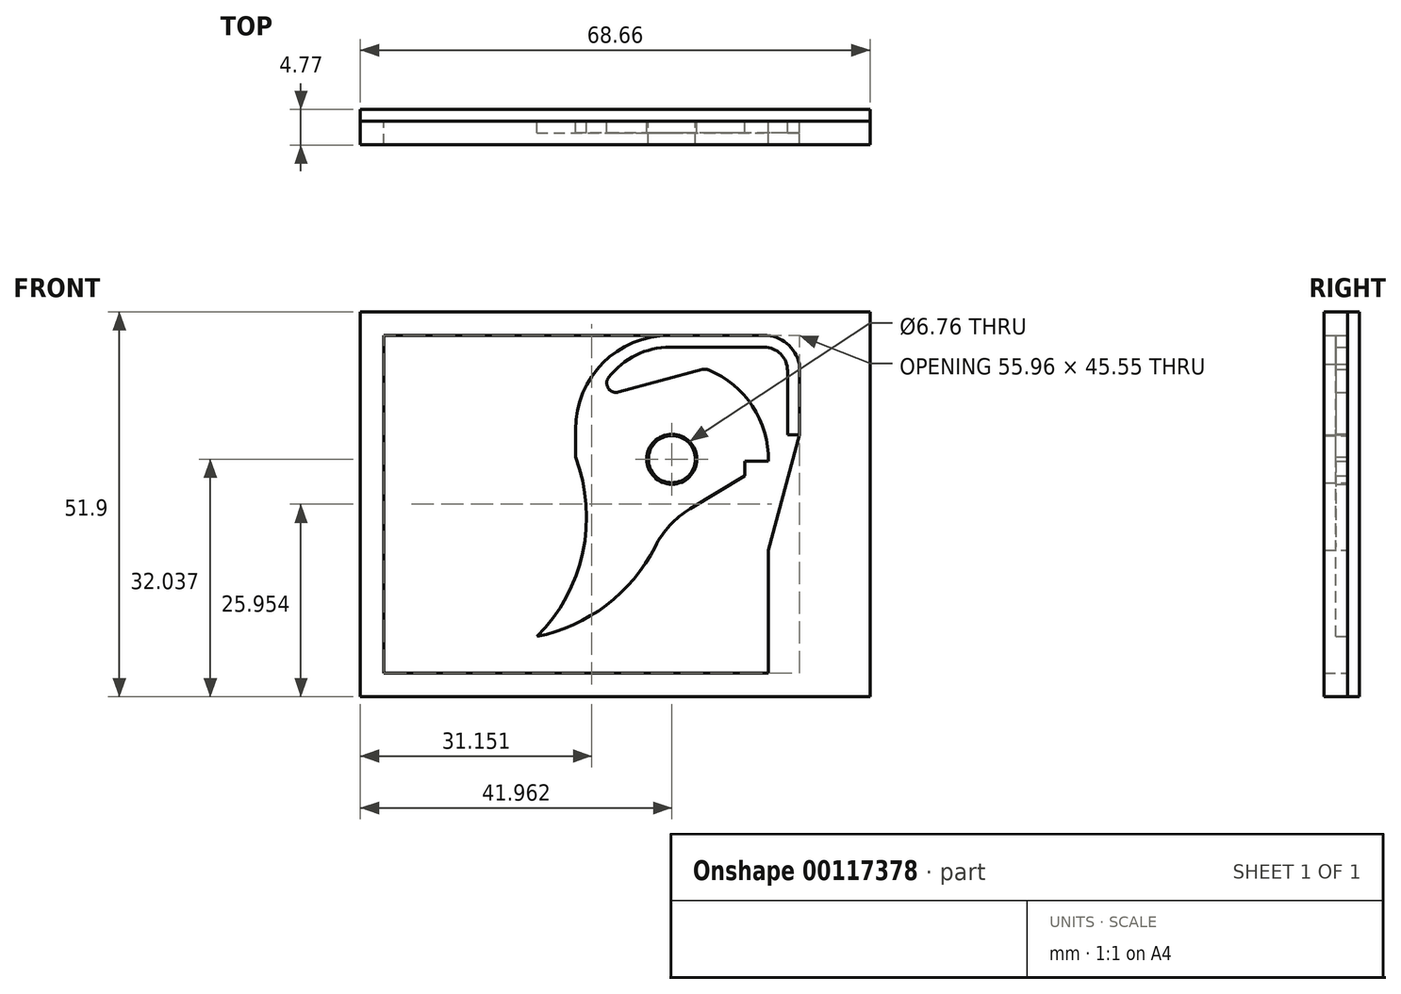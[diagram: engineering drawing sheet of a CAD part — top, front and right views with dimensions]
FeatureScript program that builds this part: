
annotation { "Feature Type Name" : "Feature", "Feature Type Description" : "" }
export const myFeature = defineFeature(function(context is Context, id is Id, definition is map)
    precondition{}
    {
        {
            var Q0;
            Q0=qCreatedBy(makeId("Front.planeOp"),FACE);
            var sketch = newSketch(context, id + "F0", { "sketchPlane" : qUnion([Q0])});
            skLineSegment(sketch, "E0.bottom", {"start": v(0, 0) * mm, "end": v(47.63, 0) * mm});
            skLineSegment(sketch, "E0.right", {"start": v(47.63, 0) * mm, "end": v(47.63, 16.58) * mm});
            skArc(sketch, "E1", {"start": v(16.43, 4.93) * mm, "mid": v(22.62, 16.26) * mm, "end": v(21.64, 29.14) * mm});
            skArc(sketch, "E2", {"start": v(16.43, 4.93) * mm, "mid": v(25.79, 9.17) * mm, "end": v(32.37, 17.06) * mm});
            skArc(sketch, "E3", {"start": v(47.62, 28.57) * mm, "mid": v(45.38, 36.16) * mm, "end": v(39.15, 41.04) * mm});
            skLineSegment(sketch, "E4", {"start": v(44.45, 26.64) * mm, "end": v(37.08, 22.15) * mm});
            skPoint(sketch, "E5.newPointB", {"position": v(34.83, 28.77) * mm});
            skArc(sketch, "E5.filletArc", {"start": v(37.08, 22.15) * mm, "mid": v(34.37, 19.93) * mm, "end": v(32.37, 17.06) * mm});
            skCircle(sketch, "E6", {"center": v(34.63, 28.86) * mm, "radius": 3.18 * mm});
            skLineSegment(sketch, "E7", {"start": v(21.64, 29.14) * mm, "end": v(21.64, 32.85) * mm});
            skLineSegment(sketch, "E8", {"start": v(34.34, 45.55) * mm, "end": v(47.04, 45.55) * mm});
            skPoint(sketch, "E9.visualSharp", {"position": v(21.64, 45.55) * mm});
            skArc(sketch, "E9.filletArc", {"start": v(34.34, 45.55) * mm, "mid": v(25.36, 41.83) * mm, "end": v(21.64, 32.85) * mm});
            skLineSegment(sketch, "E10.0", {"start": v(34.4, 43.96) * mm, "end": v(47.04, 43.96) * mm});
            skLineSegment(sketch, "E11", {"start": v(47.04, 45.55) * mm, "end": v(47.04, 43.96) * mm});
            skArc(sketch, "E12", {"start": v(34.4, 43.96) * mm, "mid": v(28.42, 42.08) * mm, "end": v(24.6, 37.11) * mm});
            skLineSegment(sketch, "E13", {"start": v(44.45, 28.58) * mm, "end": v(44.45, 26.64) * mm});
            skLineSegment(sketch, "E14", {"start": v(47.63, 28.57) * mm, "end": v(44.45, 28.57) * mm});
            skLineSegment(sketch, "E15", {"start": v(51.8, 41.64) * mm, "end": v(51.8, 32.11) * mm});
            skLineSegment(sketch, "E16.0", {"start": v(50.21, 40.79) * mm, "end": v(50.21, 32.11) * mm});
            skLineSegment(sketch, "E17", {"start": v(50.21, 32.11) * mm, "end": v(51.8, 32.11) * mm});
            skArc(sketch, "E18.filletArc", {"start": v(50.21, 40.79) * mm, "mid": v(49.28, 43.03) * mm, "end": v(47.04, 43.96) * mm});
            skArc(sketch, "E19", {"start": v(51.8, 41.64) * mm, "mid": v(50.12, 44.45) * mm, "end": v(47.04, 45.55) * mm});
            skLineSegment(sketch, "E20", {"start": v(24.6, 37.11) * mm, "end": v(39.15, 41.04) * mm});
            skLineSegment(sketch, "E21.bottom", {"start": v(-4.16, 0) * mm, "end": v(58.15, 0) * mm});
            skLineSegment(sketch, "E21.top", {"start": v(-4.16, 45.55) * mm, "end": v(58.15, 45.55) * mm});
            skLineSegment(sketch, "E21.left", {"start": v(-4.16, 0) * mm, "end": v(-4.16, 45.55) * mm});
            skLineSegment(sketch, "E21.right", {"start": v(58.15, 0) * mm, "end": v(58.15, 45.55) * mm});
            skCircle(sketch, "E22.0", {"center": v(34.63, 28.86) * mm, "radius": 3.38 * mm});
            skLineSegment(sketch, "E23", {"start": v(44.45, 26.64) * mm, "end": v(47.63, 16.58) * mm});
            skLineSegment(sketch, "E24", {"start": v(51.8, 32.11) * mm, "end": v(47.62, 16.58) * mm});
            skLineSegment(sketch, "E25.bottom", {"start": v(-7.33, -3.18) * mm, "end": v(61.33, -3.17) * mm});
            skLineSegment(sketch, "E25.top", {"start": v(-7.33, 48.72) * mm, "end": v(61.33, 48.72) * mm});
            skLineSegment(sketch, "E25.left", {"start": v(-7.33, -3.18) * mm, "end": v(-7.33, 48.72) * mm});
            skLineSegment(sketch, "E25.right", {"start": v(61.33, -3.17) * mm, "end": v(61.33, 48.72) * mm});
            skSolve(sketch);
        }
        {
            var Q0;
            Q0=makeQuery(id+"F0.imprint","IMPRINT",FACE,{"disambiguationData":[TD([[makeQuery(id+"F0.imprint","IMPRINT",EDGE,{"derivedFrom":sQuery(id+"F0.wireOp",EDGE,"E1")}),-1.0]])]});
            var Q1;
            Q1=makeQuery(id+"F0.imprint","IMPRINT",FACE,{"disambiguationData":[TD([[makeQuery(id+"F0.imprint","IMPRINT",EDGE,{"derivedFrom":sQuery(id+"F0.wireOp",EDGE,"E11")}),1.0]])]});
            extrude(context, id + "F1", {"entities" : qUnion([Q0, Q1]), "depth" : 1.59 * mm});
        }
        {
            var Q0;
            Q0=makeQuery(id+"F1.opExtrude","SWEPT_EDGE",EDGE,{"disambiguationData":[OSD([sQuery(id+"F0.wireOp",EDGE,"E3"),sQuery(id+"F0.wireOp",EDGE,"E12"),sQuery(id+"F0.wireOp",EDGE,"E20")])]});
            fillet(context, id + "F2", {"entities" : qUnion([Q0]), "radius" : 1.27 * mm, "tangentPropagation" : true, "allowEdgeOverflow" : false});
        }
        {
            var Q0;
            {var subQ0=sQuery(id+"F0.wireOp",EDGE,"E21.left");Q0=makeQuery(id+"F0.imprint","IMPRINT",FACE,{"disambiguationData":[TD([[makeQuery(id+"F0.imprint","IMPRINT",EDGE,{"derivedFrom":subQ0}),1.0]])]});}
            var Q1;
            {var subQ1=sQuery(id+"F0.wireOp",EDGE,"E0.right");Q1=makeQuery(id+"F0.imprint","IMPRINT",FACE,{"disambiguationData":[TD([[makeQuery(id+"F0.imprint","IMPRINT",EDGE,{"derivedFrom":subQ1}),-1.0]])]});}
            var Q2;
            {var subQ0=sQuery(id+"F0.wireOp",EDGE,"E0.right");Q2=makeQuery(id+"F0.imprint","IMPRINT",FACE,{"disambiguationData":[TD([[makeQuery(id+"F0.imprint","IMPRINT",EDGE,{"derivedFrom":subQ0}),1.0]])]});}
            var Q3;
            Q3=makeQuery(id+"F0.imprint","IMPRINT",FACE,{"disambiguationData":[TD([[makeQuery(id+"F0.imprint","IMPRINT",EDGE,{"derivedFrom":sQuery(id+"F0.wireOp",EDGE,"E3")}),-1.0]])]});
            var Q4;
            Q4=makeQuery(id+"F0.imprint","IMPRINT",FACE,{"disambiguationData":[TD([[makeQuery(id+"F0.imprint","IMPRINT",EDGE,{"derivedFrom":sQuery(id+"F0.wireOp",EDGE,"E6")}),-1.0]])]});
            var Q5;
            Q5=makeQuery(id+"F0.imprint","IMPRINT",FACE,{"disambiguationData":[TD([[makeQuery(id+"F0.imprint","IMPRINT",EDGE,{"derivedFrom":sQuery(id+"F0.wireOp",EDGE,"E6")}),1.0]])]});
            var Q6;
            Q6=makeQuery(id+"F0.imprint","IMPRINT",FACE,{"disambiguationData":[TD([[makeQuery(id+"F0.imprint","IMPRINT",EDGE,{"derivedFrom":sQuery(id+"F0.wireOp",EDGE,"E1")}),-1.0]])]});
            var Q7;
            Q7=makeQuery(id+"F0.imprint","IMPRINT",FACE,{"disambiguationData":[TD([[makeQuery(id+"F0.imprint","IMPRINT",EDGE,{"derivedFrom":sQuery(id+"F0.wireOp",EDGE,"E11")}),1.0]])]});
            extrude(context, id + "F3", {"entities" : qUnion([Q0, Q1, Q2, Q3, Q4, Q5, Q6, Q7]), "oppositeDirection" : true, "depth" : 1.59 * mm});
        }
        {
            var Q0;
            {var subQ0=sQuery(id+"F0.wireOp",EDGE,"E21.left");Q0=makeQuery(id+"F0.imprint","IMPRINT",FACE,{"disambiguationData":[TD([[makeQuery(id+"F0.imprint","IMPRINT",EDGE,{"derivedFrom":subQ0}),1.0]])]});}
            var Q1;
            Q1=makeQuery(id+"F0.imprint","IMPRINT",FACE,{"disambiguationData":[TD([[makeQuery(id+"F0.imprint","IMPRINT",EDGE,{"derivedFrom":sQuery(id+"F0.wireOp",EDGE,"E6")}),1.0]])]});
            var Q2;
            {var subQ1=sQuery(id+"F0.wireOp",EDGE,"E0.right");Q2=makeQuery(id+"F0.imprint","IMPRINT",FACE,{"disambiguationData":[TD([[makeQuery(id+"F0.imprint","IMPRINT",EDGE,{"derivedFrom":subQ1}),-1.0]])]});}
            extrude(context, id + "F4", {"entities" : qUnion([Q0, Q1, Q2]), "depth" : 3.17 * mm});
        }
    });
